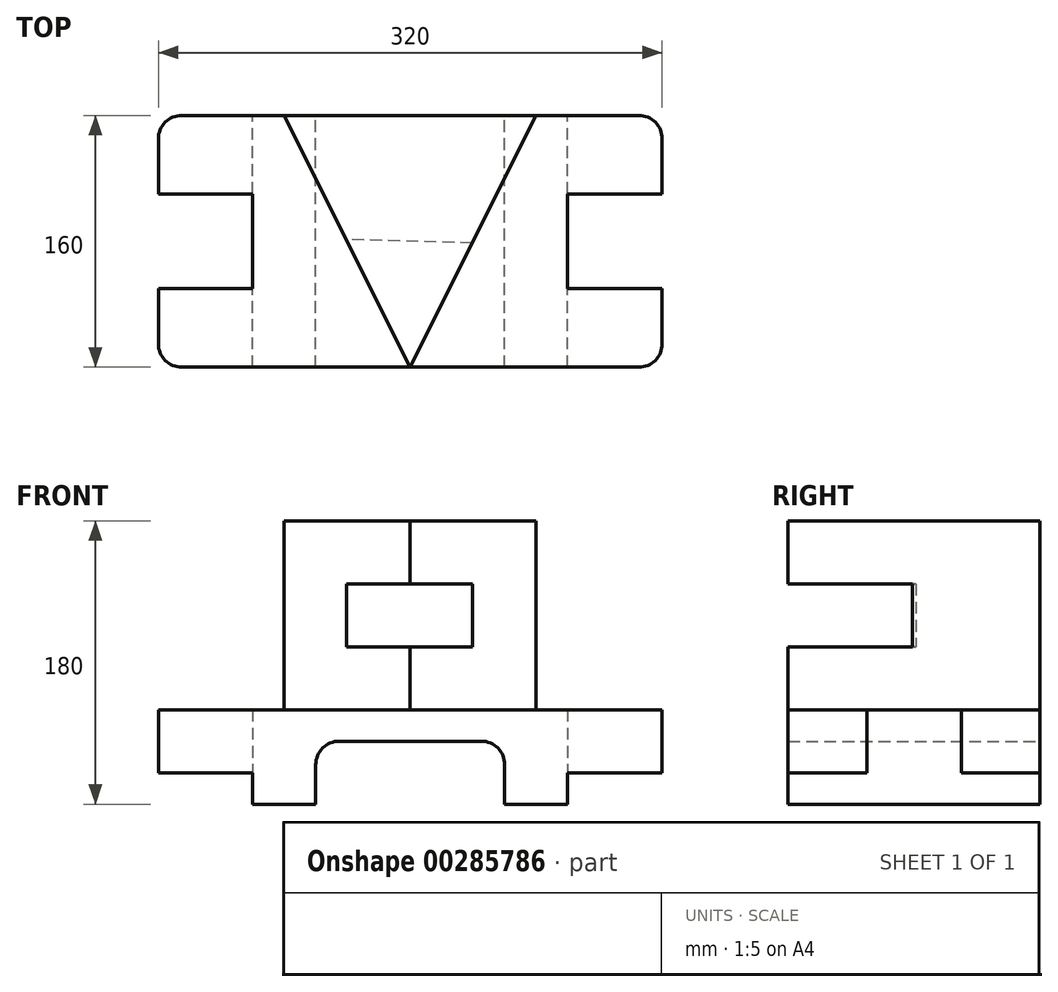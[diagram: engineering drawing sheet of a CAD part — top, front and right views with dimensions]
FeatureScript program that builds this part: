
annotation { "Feature Type Name" : "Feature", "Feature Type Description" : "" }
export const myFeature = defineFeature(function(context is Context, id is Id, definition is map)
    precondition{}
    {
        {
            var Q0;
            Q0=qCreatedBy(makeId("Top.planeOp"),FACE);
            var sketch = newSketch(context, id + "F0", { "sketchPlane" : qUnion([Q0])});
            skLineSegment(sketch, "E0", {"start": v(0, 15) * mm, "end": v(0, 50) * mm});
            skLineSegment(sketch, "E1", {"start": v(0, 50) * mm, "end": v(60, 50) * mm});
            skLineSegment(sketch, "E2", {"start": v(60, 50) * mm, "end": v(60, 110) * mm});
            skLineSegment(sketch, "E3", {"start": v(60, 110) * mm, "end": v(0, 110) * mm});
            skLineSegment(sketch, "E4", {"start": v(0, 110) * mm, "end": v(0, 145) * mm});
            skLineSegment(sketch, "E5", {"start": v(0, 160) * mm, "end": v(305, 160) * mm});
            skLineSegment(sketch, "E6", {"start": v(320, 145) * mm, "end": v(320, 110) * mm});
            skLineSegment(sketch, "E7", {"start": v(320, 110) * mm, "end": v(260, 110) * mm});
            skLineSegment(sketch, "E8", {"start": v(260, 110) * mm, "end": v(260, 50) * mm});
            skLineSegment(sketch, "E9", {"start": v(260, 50) * mm, "end": v(320, 50) * mm});
            skLineSegment(sketch, "E10", {"start": v(320, 50) * mm, "end": v(320, 15) * mm});
            skLineSegment(sketch, "E11", {"start": v(305, 0) * mm, "end": v(15, 0) * mm});
            skLineSegment(sketch, "E12", {"start": v(15, 160) * mm, "end": v(80, 160) * mm});
            skLineSegment(sketch, "E13", {"start": v(320, 160) * mm, "end": v(240, 160) * mm});
            skPoint(sketch, "E14.visualSharp", {"position": v(0, 160) * mm});
            skArc(sketch, "E14.filletArc", {"start": v(15, 160) * mm, "mid": v(4.4, 155.6) * mm, "end": v(0, 145) * mm});
            skPoint(sketch, "E15.visualSharp", {"position": v(0, 0) * mm});
            skArc(sketch, "E15.filletArc", {"start": v(0, 15) * mm, "mid": v(4.4, 4.4) * mm, "end": v(15, 0) * mm});
            skPoint(sketch, "E16.visualSharp", {"position": v(320, 0) * mm});
            skArc(sketch, "E16.filletArc", {"start": v(305, 0) * mm, "mid": v(315.6, 4.4) * mm, "end": v(320, 15) * mm});
            skPoint(sketch, "E17.visualSharp", {"position": v(320, 160) * mm});
            skArc(sketch, "E17.filletArc", {"start": v(320, 145) * mm, "mid": v(315.6, 155.6) * mm, "end": v(305, 160) * mm});
            skSolve(sketch);
        }
        {
            var Q0;
            Q0=makeQuery(id+"F0.imprint","IMPRINT",FACE,{"disambiguationData":[TD([[makeQuery(id+"F0.imprint","IMPRINT",EDGE,{"derivedFrom":sQuery(id+"F0.wireOp",EDGE,"E0")}),-1.0]])]});
            var Q1;
            Q1=makeQuery(id+"F0.imprint","IMPRINT",FACE,{"disambiguationData":[TD([[makeQuery(id+"F0.imprint","IMPRINT",EDGE,{"derivedFrom":sQuery(id+"F0.wireOp",EDGE,"E6")}),-1.0]])]});
            extrude(context, id + "F1", {"entities" : qUnion([Q0, Q1]), "endBound" : BoundingType.SYMMETRIC, "depth" : 40 * mm});
        }
        {
            var Q0;
            Q0=makeQuery(id+"F1.opExtrude","CAP_FACE",FACE,{"disambiguationData":[OSD([sQuery(id+"F0.wireOp",EDGE,"E0"),sQuery(id+"F0.wireOp",EDGE,"E1"),sQuery(id+"F0.wireOp",EDGE,"E2"),sQuery(id+"F0.wireOp",EDGE,"E3"),sQuery(id+"F0.wireOp",EDGE,"E4"),sQuery(id+"F0.wireOp",EDGE,"E5"),sQuery(id+"F0.wireOp",EDGE,"E6"),sQuery(id+"F0.wireOp",EDGE,"E7"),sQuery(id+"F0.wireOp",EDGE,"E8"),sQuery(id+"F0.wireOp",EDGE,"E9"),sQuery(id+"F0.wireOp",EDGE,"E10"),sQuery(id+"F0.wireOp",EDGE,"E11"),sQuery(id+"F0.wireOp",EDGE,"E12"),sQuery(id+"F0.wireOp",EDGE,"E13"),sQuery(id+"F0.wireOp",EDGE,"E14.filletArc"),sQuery(id+"F0.wireOp",EDGE,"E15.filletArc"),sQuery(id+"F0.wireOp",EDGE,"E16.filletArc"),sQuery(id+"F0.wireOp",EDGE,"E17.filletArc")])],"isStart":false});
            var sketch = newSketch(context, id + "F2", { "sketchPlane" : qUnion([Q0])});
            skLineSegment(sketch, "E18", {"start": v(160, 160) * mm, "end": v(240, 160) * mm});
            skLineSegment(sketch, "E19", {"start": v(160, 160) * mm, "end": v(80, 160) * mm});
            skLineSegment(sketch, "E20", {"start": v(80, 160) * mm, "end": v(160, 0) * mm});
            skLineSegment(sketch, "E21", {"start": v(160, 0) * mm, "end": v(240, 160) * mm});
            skSolve(sketch);
        }
        {
            var Q0;
            Q0=makeQuery(id+"F2.imprint","IMPRINT",FACE,{"disambiguationData":[TD([[makeQuery(id+"F2.imprint","IMPRINT",EDGE,{"derivedFrom":sQuery(id+"F2.wireOp",EDGE,"E18")}),-1.0]])]});
            extrude(context, id + "F3", {"entities" : qUnion([Q0]), "operationType" : NewBodyOperationType.ADD, "depth" : 120 * mm});
        }
        {
            var Q0;
            Q0=makeQuery(id+"F0.imprint","IMPRINT",FACE,{"disambiguationData":[TD([[makeQuery(id+"F0.imprint","IMPRINT",EDGE,{"derivedFrom":sQuery(id+"F0.wireOp",EDGE,"E0")}),-1.0]])]});
            var sketch = newSketch(context, id + "F4", { "sketchPlane" : qUnion([Q0])});
            skLineSegment(sketch, "E22.bottom", {"start": v(60, 0) * mm, "end": v(260, 0) * mm});
            skLineSegment(sketch, "E22.top", {"start": v(60, 160) * mm, "end": v(260, 160) * mm});
            skLineSegment(sketch, "E22.left", {"start": v(60, 0) * mm, "end": v(60, 160) * mm});
            skLineSegment(sketch, "E22.right", {"start": v(260, 0) * mm, "end": v(260, 160) * mm});
            skSolve(sketch);
        }
        {
            var Q0;
            {var subQ8=sQuery(id+"F4.wireOp",EDGE,"E22.bottom");Q0=makeQuery(id+"F4.imprint","IMPRINT",FACE,{"disambiguationData":[TD([[makeQuery(id+"F4.imprint","IMPRINT",EDGE,{"derivedFrom":subQ8}),-1.0]])]});}
            extrude(context, id + "F5", {"entities" : qUnion([Q0]), "operationType" : NewBodyOperationType.ADD, "oppositeDirection" : true, "depth" : 40 * mm});
        }
        {
            var Q0;
            Q0=makeQuery(id+"F5.boolean.opBoolean","MERGE",FACE,{"derivedFrom":[makeQuery(id+"F3.boolean.opBoolean","MERGE",FACE,{"derivedFrom":[makeQuery(id+"F1.opExtrude","SWEPT_FACE",FACE,{"disambiguationData":[OSD([sQuery(id+"F0.wireOp",EDGE,"E5"),sQuery(id+"F0.wireOp",EDGE,"E12"),sQuery(id+"F0.wireOp",EDGE,"E13")])]}),makeQuery(id+"F3.opExtrude","SWEPT_FACE",FACE,{"disambiguationData":[OSD([sQuery(id+"F2.wireOp",EDGE,"E18"),sQuery(id+"F2.wireOp",EDGE,"E19")])]})]}),makeQuery(id+"F5.opExtrude","SWEPT_FACE",FACE,{"disambiguationData":[OSD([sQuery(id+"F4.wireOp",EDGE,"E22.top")])]})]});
            var sketch = newSketch(context, id + "F6", { "sketchPlane" : qUnion([Q0])});
            skLineSegment(sketch, "E23", {"start": v(-60, -40) * mm, "end": v(-100, -40) * mm});
            skLineSegment(sketch, "E24", {"start": v(-260, -40) * mm, "end": v(-220, -40) * mm});
            skLineSegment(sketch, "E25", {"start": v(-100, -40) * mm, "end": v(-100, -15) * mm});
            skLineSegment(sketch, "E26", {"start": v(-115, 0) * mm, "end": v(-205, 0) * mm});
            skLineSegment(sketch, "E27", {"start": v(-220, -15) * mm, "end": v(-220, -40) * mm});
            skPoint(sketch, "E28.visualSharp", {"position": v(-100, 0) * mm});
            skArc(sketch, "E28.filletArc", {"start": v(-100, -15) * mm, "mid": v(-104.4, -4.4) * mm, "end": v(-115, 0) * mm});
            skPoint(sketch, "E29.visualSharp", {"position": v(-220, 0) * mm});
            skArc(sketch, "E29.filletArc", {"start": v(-205, 0) * mm, "mid": v(-215.6, -4.4) * mm, "end": v(-220, -15) * mm});
            skSolve(sketch);
        }
        {
            var Q0;
            Q0 = qSketchRegion(id + "F6", true);
            var Q1;
            {var subQ0=sQuery(id+"F6.wireOp",EDGE,"E25");Q1=makeQuery(id+"F6.imprint","IMPRINT",FACE,{"disambiguationData":[TD([[makeQuery(id+"F6.imprint","IMPRINT",EDGE,{"derivedFrom":subQ0}),1.0]])]});}
            extrude(context, id + "F7", {"entities" : qUnion([Q0, Q1]), "operationType" : NewBodyOperationType.REMOVE, "endBound" : BoundingType.THROUGH_ALL, "oppositeDirection" : true, "depth" : 25 * mm});
        }
        {
            var Q0;
            Q0=makeQuery(id+"F3.opExtrude","SWEPT_EDGE",EDGE,{"disambiguationData":[OSD([sQuery(id+"F0.wireOp",EDGE,"E11"),sQuery(id+"F2.wireOp",EDGE,"E20"),sQuery(id+"F2.wireOp",EDGE,"E21")])]});
            var Q1;
            Q1=makeQuery(id+"F3.opExtrude","SWEPT_FACE",FACE,{"disambiguationData":[OSD([sQuery(id+"F2.wireOp",EDGE,"E21")])]});
            cPlane(context, id + "F8", {"entities" : qUnion([Q0, Q1]), "cplaneType" : CPlaneType.LINE_ANGLE, "offset" : 25 * mm, "angle" : 155 * degree, "width" : 150 * mm, "height" : 150 * mm});
        }
        {
            var Q0;
            Q0=qCreatedBy(id+"F8.planeOp",FACE);
            var sketch = newSketch(context, id + "F9", { "sketchPlane" : qUnion([Q0])});
            skLineSegment(sketch, "E30.0", {"start": v(4.37, 60) * mm, "end": v(4.37, 20) * mm});
            skLineSegment(sketch, "E31", {"start": v(4.37, 20) * mm, "end": v(4.37, 60) * mm, "construction": true});
            skPoint(sketch, "E32.orphan", {"position": v(4.37, 140) * mm});
            skLineSegment(sketch, "E33.bottom", {"start": v(4.37, 60) * mm, "end": v(84.37, 60) * mm});
            skLineSegment(sketch, "E33.top", {"start": v(4.37, 100) * mm, "end": v(84.37, 100) * mm});
            skLineSegment(sketch, "E33.left", {"start": v(4.37, 60) * mm, "end": v(4.37, 100) * mm});
            skLineSegment(sketch, "E33.right", {"start": v(84.37, 60) * mm, "end": v(84.37, 100) * mm});
            skSolve(sketch);
        }
        {
            var Q0;
            Q0 = qSketchRegion(id + "F9", true);
            extrude(context, id + "F10", {"entities" : qUnion([Q0]), "operationType" : NewBodyOperationType.REMOVE, "endBound" : BoundingType.THROUGH_ALL, "depth" : 25 * mm, "hasSecondDirection" : true, "secondDirectionBound" : SecondDirectionBoundingType.THROUGH_ALL, "secondDirectionOppositeDirection" : true, "secondDirectionDepth" : 25 * mm});
        }
    });
